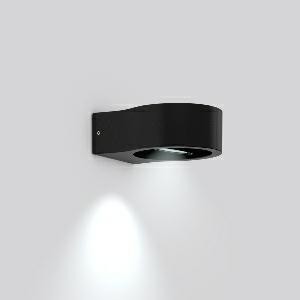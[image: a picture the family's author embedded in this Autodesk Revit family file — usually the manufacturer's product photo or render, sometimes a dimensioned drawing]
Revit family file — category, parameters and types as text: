
# Revit family: hb_102_611981_0031_3097
name_source: partatom
category: Lighting Fixtures
units: mm (PartAtom-declared; Revit-internal decimal feet)

## family parameters
Cut with Voids When Loaded = No
Host = Face
Light Source = No
Part Type = Normal
Room Calculation Point = No
Round Connector Dimension = Use Diameter
Shared = No

## types (1)
- HB 102 (1 x LED Modul 830, 270 lm, 3000)
    Apparent Load = 6 VA
    CIE Flux Codes = 96 99 100 99 100
    Color Rendering = 80
    Color Temperature = 3000
    Default Elevation = 1800 mm
    Description = Series: HB 102
Wall luminaire. Housing: die-cast aluminium, powder-coated. Swivel spot. Light emission: one side. Driver integrated. 
Colour: anthracite metallic (DB703)
Length: 110 mm
Width: 161 mm
Height: 55 mm
Lamp: LED
System power: 6 W
Rated luminous flux: 270 lm
Luminous efficiency: 45 lm/W
Control gear: Regulated power supply
Protection class: I
Type of protection: IP 54
    Height = 55 mm
    Lamp = 1 x LED Modul 830
    Lamp Light Flux = 270 lm
    Lamp count = 1
    Length = 110 mm
    Lifetime = 50000 h
    Luminous efficacy = 45 lm/W
    Manufacturer = RZB
    ModVariant = No
    Model = 611981.0031
    Mounting Place = Wall
    Mounting Type = Surface mounted
    Number of Poles = 1
    OnlyDefault = Yes
    Power Factor = 1
    Product Name = HB 102
    Product group = Surface mounted Wall luminaires
    ProductGroupID = 2001
    Protection Class = Protection class I
    Protection Degree = IP 54
    RLX_Detail_Level = 1
    RLX_Emergency_Light_Flux = 0 lm
    RLX_Emergency_Type = 0
    RLX_Emergency_Type_DB = No
    RlxData = <blob elided: 57037 chars, md5=c1b36248>
    Socket = socket
    Standby Power = 0 W
    System Light Flux = 270 lm
    System Power = 6 W
    Type Comments = Product without accessories
    Type Image = 611981.0031.jpg
    URL = http://relux.com
    VarID = ---
    Voltage = 0 V
    Weight = 0.00 kg
    Width = 161 mm

## geometry (parser evidence)
native form markers: Blend x4, Sweep x14
no freeform markers — native parametric forms only
